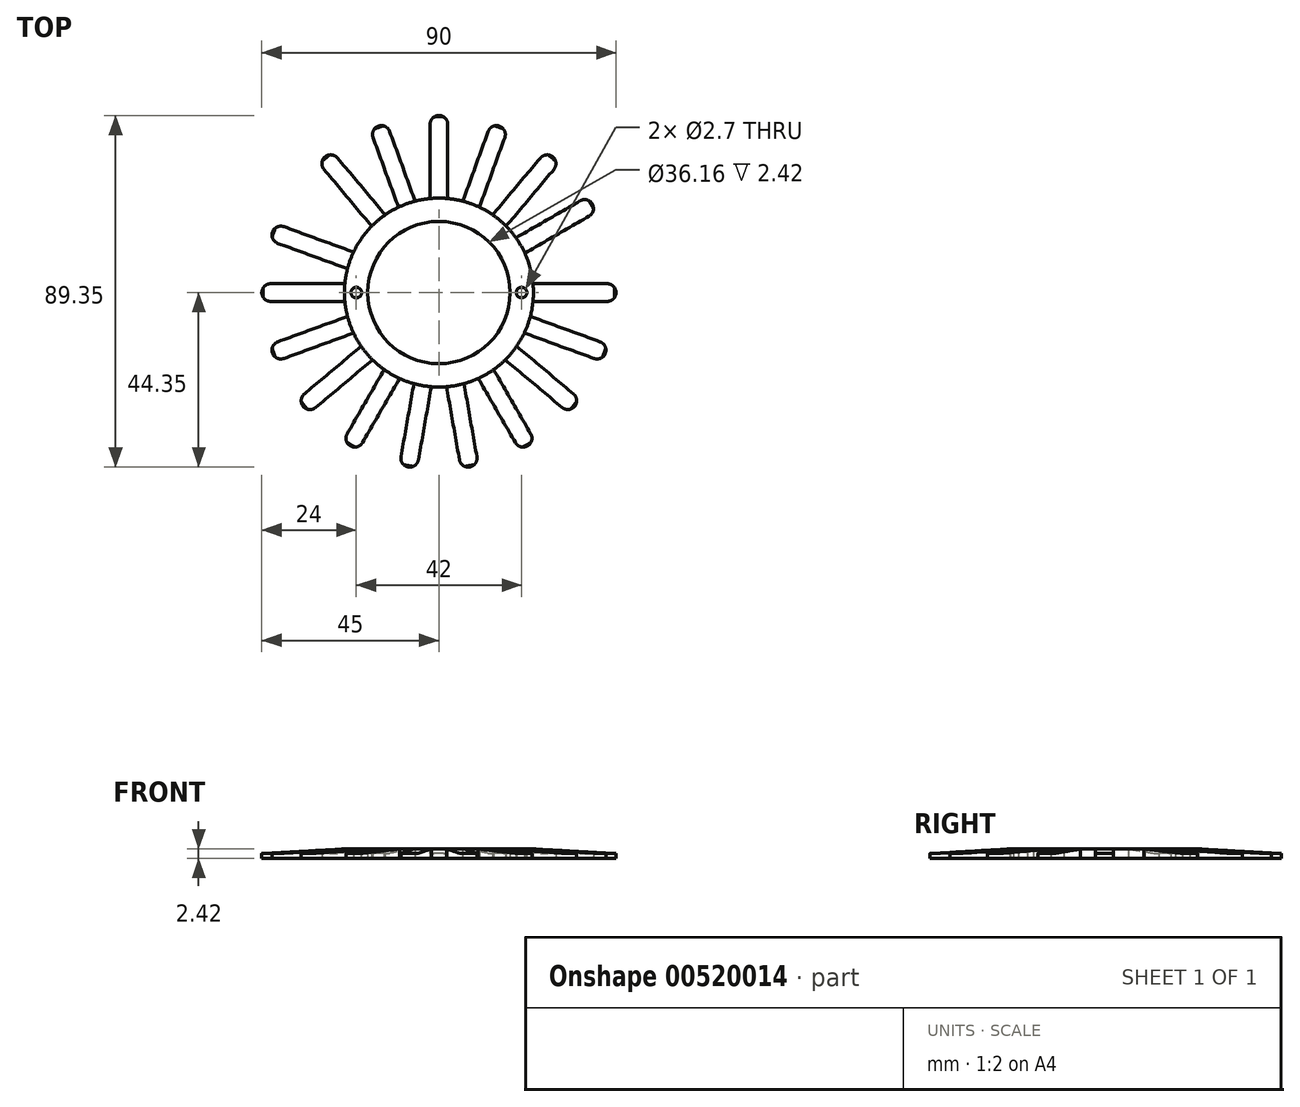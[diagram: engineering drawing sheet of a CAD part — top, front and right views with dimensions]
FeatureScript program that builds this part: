
annotation { "Feature Type Name" : "Feature", "Feature Type Description" : "" }
export const myFeature = defineFeature(function(context is Context, id is Id, definition is map)
    precondition{}
    {
        {
            var Q0;
            Q0=qCreatedBy(makeId("Top.planeOp"),FACE);
            var sketch = newSketch(context, id + "F0", { "sketchPlane" : qUnion([Q0])});
            skCircle(sketch, "E0", {"center": v(0, 0) * mm, "radius": 6.03 * mm});
            skCircle(sketch, "E1", {"center": v(0, 0) * mm, "radius": 8 * mm});
            skSolve(sketch);
        }
        {
            var Q0;
            Q0=makeQuery(id+"F0.imprint","IMPRINT",FACE,{"disambiguationData":[TD([[makeQuery(id+"F0.imprint","IMPRINT",EDGE,{"derivedFrom":sQuery(id+"F0.wireOp",EDGE,"E0")}),-1.0]])]});
            extrude(context, id + "F1", {"entities" : qUnion([Q0]), "depth" : 0.34 * mm});
        }
        {
            var Q0;
            Q0=qCreatedBy(makeId("Top.planeOp"),FACE);
            var sketch = newSketch(context, id + "F2", { "sketchPlane" : qUnion([Q0])});
            skCircle(sketch, "E2", {"center": v(0, 0) * mm, "radius": 8 * mm, "construction": true});
            skCircle(sketch, "E3", {"center": v(0, 0) * mm, "radius": 15 * mm, "construction": true});
            skArc(sketch, "E4", {"start": v(14.25, -0.75) * mm, "mid": v(15, 0) * mm, "end": v(14.25, 0.75) * mm});
            skLineSegment(sketch, "E5", {"start": v(14.25, -0.75) * mm, "end": v(7.96, -0.75) * mm});
            skLineSegment(sketch, "E6", {"start": v(14.25, 0.75) * mm, "end": v(7.96, 0.75) * mm});
            skLineSegment(sketch, "E7", {"start": v(7.96, 0.75) * mm, "end": v(7.96, -0.75) * mm});
            skSolve(sketch);
        }
        {
            var Q0;
            Q0=makeQuery(id+"F2.imprint","IMPRINT",FACE,{"disambiguationData":[TD([[makeQuery(id+"F2.imprint","IMPRINT",EDGE,{"derivedFrom":sQuery(id+"F2.wireOp",EDGE,"E4")}),1.0]])]});
            extrude(context, id + "F3", {"entities" : qUnion([Q0]), "depth" : 0.34 * mm});
        }
        {
            var Q0;
            Q0=qCreatedBy(makeId("Front.planeOp"),FACE);
            var sketch = newSketch(context, id + "F4", { "sketchPlane" : qUnion([Q0])});
            skLineSegment(sketch, "E8", {"start": v(0, 0) * mm, "end": v(0, 5.33) * mm, "construction": true});
            skSolve(sketch);
        }
        {
            var Q0;
            Q0=makeQuery(id+"F3.opExtrude","SWEPT_BODY",BODY,{"disambiguationData":[OSD([sQuery(id+"F2.wireOp",EDGE,"E4"),sQuery(id+"F2.wireOp",EDGE,"E5"),sQuery(id+"F2.wireOp",EDGE,"E6"),sQuery(id+"F2.wireOp",EDGE,"E7")])]});
            var Q1;
            Q1=sQuery(id+"F4.wireOp",EDGE,"E8");
            circularPattern(context, id + "F5", {"entities" : qUnion([Q0]), "axis" : qUnion([Q1]), "angle" : 20 * degree, "instanceCount" : 11, "oppositeDirection" : true});
        }
        {
            var Q0;
            Q0=qCreatedBy(makeId("Top.planeOp"),FACE);
            var sketch = newSketch(context, id + "F6", { "sketchPlane" : qUnion([Q0])});
            skCircle(sketch, "E9", {"center": v(0, 0) * mm, "radius": 15 * mm, "construction": true});
            skLineSegment(sketch, "E10", {"start": v(0, 0) * mm, "end": v(13, 7.5) * mm, "construction": true});
            skLineSegment(sketch, "E11", {"start": v(0, 0) * mm, "end": v(13.86, 0) * mm, "construction": true});
            skArc(sketch, "E12", {"start": v(12.72, 6.48) * mm, "mid": v(13, 7.5) * mm, "end": v(11.97, 7.77) * mm});
            skLineSegment(sketch, "E13", {"start": v(12.34, 7.13) * mm, "end": v(12.72, 6.48) * mm});
            skLineSegment(sketch, "E14", {"start": v(12.72, 6.48) * mm, "end": v(6.65, 2.98) * mm});
            skLineSegment(sketch, "E15", {"start": v(6.65, 2.98) * mm, "end": v(5.9, 4.27) * mm});
            skLineSegment(sketch, "E16", {"start": v(5.9, 4.27) * mm, "end": v(11.97, 7.77) * mm});
            skSolve(sketch);
        }
        {
            var Q0;
            Q0=makeQuery(id+"F6.imprint","IMPRINT",FACE,{"disambiguationData":[TD([[makeQuery(id+"F6.imprint","IMPRINT",EDGE,{"derivedFrom":sQuery(id+"F6.wireOp",EDGE,"E12")}),1.0]])]});
            extrude(context, id + "F7", {"entities" : qUnion([Q0]), "depth" : 0.34 * mm});
        }
        {
            var Q0;
            Q0=makeQuery(id+"F7.opExtrude","SWEPT_BODY",BODY,{"disambiguationData":[OSD([sQuery(id+"F6.wireOp",EDGE,"E12"),sQuery(id+"F6.wireOp",EDGE,"E14"),sQuery(id+"F6.wireOp",EDGE,"E15"),sQuery(id+"F6.wireOp",EDGE,"E16")])]});
            var Q1;
            Q1=sQuery(id+"F4.wireOp",EDGE,"E8");
            circularPattern(context, id + "F8", {"entities" : qUnion([Q0]), "axis" : qUnion([Q1]), "angle" : 20 * degree, "instanceCount" : 6});
        }
        {
            var Q0;
            Q0=makeQuery(id+"F1.opExtrude","SWEPT_BODY",BODY,{"disambiguationData":[OSD([sQuery(id+"F0.wireOp",EDGE,"E0"),sQuery(id+"F0.wireOp",EDGE,"E1")])]});
            var Q1;
            Q1=makeQuery(id+"F7.opExtrude","SWEPT_BODY",BODY,{"disambiguationData":[OSD([sQuery(id+"F6.wireOp",EDGE,"E12"),sQuery(id+"F6.wireOp",EDGE,"E14"),sQuery(id+"F6.wireOp",EDGE,"E15"),sQuery(id+"F6.wireOp",EDGE,"E16")])]});
            var Q2;
            Q2=makeQuery(id+"F8.opPattern","COPY",BODY,{"derivedFrom":makeQuery(id+"F7.opExtrude","SWEPT_BODY",BODY,{"disambiguationData":[OSD([sQuery(id+"F6.wireOp",EDGE,"E12"),sQuery(id+"F6.wireOp",EDGE,"E14"),sQuery(id+"F6.wireOp",EDGE,"E15"),sQuery(id+"F6.wireOp",EDGE,"E16")])]}),"instanceName":"1"});
            var Q3;
            Q3=makeQuery(id+"F8.opPattern","COPY",BODY,{"derivedFrom":makeQuery(id+"F7.opExtrude","SWEPT_BODY",BODY,{"disambiguationData":[OSD([sQuery(id+"F6.wireOp",EDGE,"E12"),sQuery(id+"F6.wireOp",EDGE,"E14"),sQuery(id+"F6.wireOp",EDGE,"E15"),sQuery(id+"F6.wireOp",EDGE,"E16")])]}),"instanceName":"2"});
            var Q4;
            Q4=makeQuery(id+"F8.opPattern","COPY",BODY,{"derivedFrom":makeQuery(id+"F7.opExtrude","SWEPT_BODY",BODY,{"disambiguationData":[OSD([sQuery(id+"F6.wireOp",EDGE,"E12"),sQuery(id+"F6.wireOp",EDGE,"E14"),sQuery(id+"F6.wireOp",EDGE,"E15"),sQuery(id+"F6.wireOp",EDGE,"E16")])]}),"instanceName":"3"});
            var Q5;
            Q5=makeQuery(id+"F8.opPattern","COPY",BODY,{"derivedFrom":makeQuery(id+"F7.opExtrude","SWEPT_BODY",BODY,{"disambiguationData":[OSD([sQuery(id+"F6.wireOp",EDGE,"E12"),sQuery(id+"F6.wireOp",EDGE,"E14"),sQuery(id+"F6.wireOp",EDGE,"E15"),sQuery(id+"F6.wireOp",EDGE,"E16")])]}),"instanceName":"4"});
            var Q6;
            Q6=makeQuery(id+"F8.opPattern","COPY",BODY,{"derivedFrom":makeQuery(id+"F7.opExtrude","SWEPT_BODY",BODY,{"disambiguationData":[OSD([sQuery(id+"F6.wireOp",EDGE,"E12"),sQuery(id+"F6.wireOp",EDGE,"E14"),sQuery(id+"F6.wireOp",EDGE,"E15"),sQuery(id+"F6.wireOp",EDGE,"E16")])]}),"instanceName":"5"});
            var Q7;
            Q7=makeQuery(id+"F5.opPattern","COPY",BODY,{"derivedFrom":makeQuery(id+"F3.opExtrude","SWEPT_BODY",BODY,{"disambiguationData":[OSD([sQuery(id+"F2.wireOp",EDGE,"E4"),sQuery(id+"F2.wireOp",EDGE,"E5"),sQuery(id+"F2.wireOp",EDGE,"E6"),sQuery(id+"F2.wireOp",EDGE,"E7")])]}),"instanceName":"10"});
            var Q8;
            Q8=makeQuery(id+"F5.opPattern","COPY",BODY,{"derivedFrom":makeQuery(id+"F3.opExtrude","SWEPT_BODY",BODY,{"disambiguationData":[OSD([sQuery(id+"F2.wireOp",EDGE,"E4"),sQuery(id+"F2.wireOp",EDGE,"E5"),sQuery(id+"F2.wireOp",EDGE,"E6"),sQuery(id+"F2.wireOp",EDGE,"E7")])]}),"instanceName":"9"});
            var Q9;
            Q9=makeQuery(id+"F5.opPattern","COPY",BODY,{"derivedFrom":makeQuery(id+"F3.opExtrude","SWEPT_BODY",BODY,{"disambiguationData":[OSD([sQuery(id+"F2.wireOp",EDGE,"E4"),sQuery(id+"F2.wireOp",EDGE,"E5"),sQuery(id+"F2.wireOp",EDGE,"E6"),sQuery(id+"F2.wireOp",EDGE,"E7")])]}),"instanceName":"8"});
            var Q10;
            Q10=makeQuery(id+"F5.opPattern","COPY",BODY,{"derivedFrom":makeQuery(id+"F3.opExtrude","SWEPT_BODY",BODY,{"disambiguationData":[OSD([sQuery(id+"F2.wireOp",EDGE,"E4"),sQuery(id+"F2.wireOp",EDGE,"E5"),sQuery(id+"F2.wireOp",EDGE,"E6"),sQuery(id+"F2.wireOp",EDGE,"E7")])]}),"instanceName":"7"});
            var Q11;
            Q11=makeQuery(id+"F5.opPattern","COPY",BODY,{"derivedFrom":makeQuery(id+"F3.opExtrude","SWEPT_BODY",BODY,{"disambiguationData":[OSD([sQuery(id+"F2.wireOp",EDGE,"E4"),sQuery(id+"F2.wireOp",EDGE,"E5"),sQuery(id+"F2.wireOp",EDGE,"E6"),sQuery(id+"F2.wireOp",EDGE,"E7")])]}),"instanceName":"6"});
            var Q12;
            Q12=makeQuery(id+"F5.opPattern","COPY",BODY,{"derivedFrom":makeQuery(id+"F3.opExtrude","SWEPT_BODY",BODY,{"disambiguationData":[OSD([sQuery(id+"F2.wireOp",EDGE,"E4"),sQuery(id+"F2.wireOp",EDGE,"E5"),sQuery(id+"F2.wireOp",EDGE,"E6"),sQuery(id+"F2.wireOp",EDGE,"E7")])]}),"instanceName":"4"});
            var Q13;
            Q13=makeQuery(id+"F5.opPattern","COPY",BODY,{"derivedFrom":makeQuery(id+"F3.opExtrude","SWEPT_BODY",BODY,{"disambiguationData":[OSD([sQuery(id+"F2.wireOp",EDGE,"E4"),sQuery(id+"F2.wireOp",EDGE,"E5"),sQuery(id+"F2.wireOp",EDGE,"E6"),sQuery(id+"F2.wireOp",EDGE,"E7")])]}),"instanceName":"5"});
            var Q14;
            Q14=makeQuery(id+"F5.opPattern","COPY",BODY,{"derivedFrom":makeQuery(id+"F3.opExtrude","SWEPT_BODY",BODY,{"disambiguationData":[OSD([sQuery(id+"F2.wireOp",EDGE,"E4"),sQuery(id+"F2.wireOp",EDGE,"E5"),sQuery(id+"F2.wireOp",EDGE,"E6"),sQuery(id+"F2.wireOp",EDGE,"E7")])]}),"instanceName":"3"});
            var Q15;
            Q15=makeQuery(id+"F5.opPattern","COPY",BODY,{"derivedFrom":makeQuery(id+"F3.opExtrude","SWEPT_BODY",BODY,{"disambiguationData":[OSD([sQuery(id+"F2.wireOp",EDGE,"E4"),sQuery(id+"F2.wireOp",EDGE,"E5"),sQuery(id+"F2.wireOp",EDGE,"E6"),sQuery(id+"F2.wireOp",EDGE,"E7")])]}),"instanceName":"2"});
            var Q16;
            Q16=makeQuery(id+"F5.opPattern","COPY",BODY,{"derivedFrom":makeQuery(id+"F3.opExtrude","SWEPT_BODY",BODY,{"disambiguationData":[OSD([sQuery(id+"F2.wireOp",EDGE,"E4"),sQuery(id+"F2.wireOp",EDGE,"E5"),sQuery(id+"F2.wireOp",EDGE,"E6"),sQuery(id+"F2.wireOp",EDGE,"E7")])]}),"instanceName":"1"});
            var Q17;
            Q17=makeQuery(id+"F3.opExtrude","SWEPT_BODY",BODY,{"disambiguationData":[OSD([sQuery(id+"F2.wireOp",EDGE,"E4"),sQuery(id+"F2.wireOp",EDGE,"E5"),sQuery(id+"F2.wireOp",EDGE,"E6"),sQuery(id+"F2.wireOp",EDGE,"E7")])]});
            booleanBodies(context, id + "F9", {"operationType" : BooleanOperationType.UNION, "tools" : qUnion([Q0, Q1, Q2, Q3, Q4, Q5, Q6, Q7, Q8, Q9, Q10, Q11, Q12, Q13, Q14, Q15, Q16, Q17])});
        }
        {
            var Q0;
            {var subQ0=makeQuery(id+"F3.opExtrude","CAP_FACE",FACE,{"disambiguationData":[OSD([sQuery(id+"F2.wireOp",EDGE,"E4"),sQuery(id+"F2.wireOp",EDGE,"E5"),sQuery(id+"F2.wireOp",EDGE,"E6"),sQuery(id+"F2.wireOp",EDGE,"E7")])],"isStart":false});var subQ1=makeQuery(id+"F7.opExtrude","CAP_FACE",FACE,{"disambiguationData":[OSD([sQuery(id+"F6.wireOp",EDGE,"E12"),sQuery(id+"F6.wireOp",EDGE,"E14"),sQuery(id+"F6.wireOp",EDGE,"E15"),sQuery(id+"F6.wireOp",EDGE,"E16")])],"isStart":false});Q0=makeQuery(id+"F9.opBoolean","MERGE",FACE,{"derivedFrom":[makeQuery(id+"F1.opExtrude","CAP_FACE",FACE,{"disambiguationData":[OSD([sQuery(id+"F0.wireOp",EDGE,"E0"),sQuery(id+"F0.wireOp",EDGE,"E1")])],"isStart":false}),subQ0,makeQuery(id+"F5.opPattern","COPY",FACE,{"derivedFrom":subQ0,"instanceName":"1"}),makeQuery(id+"F5.opPattern","COPY",FACE,{"derivedFrom":subQ0,"instanceName":"2"}),makeQuery(id+"F5.opPattern","COPY",FACE,{"derivedFrom":subQ0,"instanceName":"3"}),makeQuery(id+"F5.opPattern","COPY",FACE,{"derivedFrom":subQ0,"instanceName":"4"}),makeQuery(id+"F5.opPattern","COPY",FACE,{"derivedFrom":subQ0,"instanceName":"5"}),makeQuery(id+"F5.opPattern","COPY",FACE,{"derivedFrom":subQ0,"instanceName":"6"}),makeQuery(id+"F5.opPattern","COPY",FACE,{"derivedFrom":subQ0,"instanceName":"7"}),makeQuery(id+"F5.opPattern","COPY",FACE,{"derivedFrom":subQ0,"instanceName":"8"}),makeQuery(id+"F5.opPattern","COPY",FACE,{"derivedFrom":subQ0,"instanceName":"9"}),makeQuery(id+"F5.opPattern","COPY",FACE,{"derivedFrom":subQ0,"instanceName":"10"}),subQ1,makeQuery(id+"F8.opPattern","COPY",FACE,{"derivedFrom":subQ1,"instanceName":"1"}),makeQuery(id+"F8.opPattern","COPY",FACE,{"derivedFrom":subQ1,"instanceName":"2"}),makeQuery(id+"F8.opPattern","COPY",FACE,{"derivedFrom":subQ1,"instanceName":"3"}),makeQuery(id+"F8.opPattern","COPY",FACE,{"derivedFrom":subQ1,"instanceName":"4"}),makeQuery(id+"F8.opPattern","COPY",FACE,{"derivedFrom":subQ1,"instanceName":"5"})]});}
            var sketch = newSketch(context, id + "F10", { "sketchPlane" : qUnion([Q0])});
            skCircle(sketch, "E17", {"center": v(0, 0) * mm, "radius": 7 * mm, "construction": true});
            skCircle(sketch, "E18", {"center": v(7, 0) * mm, "radius": 0.45 * mm});
            skCircle(sketch, "E19", {"center": v(-7, 0) * mm, "radius": 0.45 * mm});
            skSolve(sketch);
        }
        {
            var Q0;
            {Q0=qUnion([makeQuery(id+"F10.imprint","IMPRINT",FACE,{"disambiguationData":[TD([[makeQuery(id+"F10.imprint","IMPRINT",EDGE,{"derivedFrom":sQuery(id+"F10.wireOp",EDGE,"E18")}),1.0]])]}),makeQuery(id+"F10.imprint","IMPRINT",FACE,{"disambiguationData":[TD([[makeQuery(id+"F10.imprint","IMPRINT",EDGE,{"derivedFrom":sQuery(id+"F10.wireOp",EDGE,"E19")}),1.0]])]})]);}
            var Q2;
            {var subQ0=makeQuery(id+"F7.opExtrude","CAP_FACE",FACE,{"disambiguationData":[OSD([sQuery(id+"F6.wireOp",EDGE,"E12"),sQuery(id+"F6.wireOp",EDGE,"E14"),sQuery(id+"F6.wireOp",EDGE,"E15"),sQuery(id+"F6.wireOp",EDGE,"E16")])],"isStart":true});var subQ1=makeQuery(id+"F3.opExtrude","CAP_FACE",FACE,{"disambiguationData":[OSD([sQuery(id+"F2.wireOp",EDGE,"E4"),sQuery(id+"F2.wireOp",EDGE,"E5"),sQuery(id+"F2.wireOp",EDGE,"E6"),sQuery(id+"F2.wireOp",EDGE,"E7")])],"isStart":true});Q2=makeQuery(id+"F9.opBoolean","MERGE",FACE,{"derivedFrom":[makeQuery(id+"F1.opExtrude","CAP_FACE",FACE,{"disambiguationData":[OSD([sQuery(id+"F0.wireOp",EDGE,"E0"),sQuery(id+"F0.wireOp",EDGE,"E1")])],"isStart":true}),subQ1,makeQuery(id+"F5.opPattern","COPY",FACE,{"derivedFrom":subQ1,"instanceName":"1"}),makeQuery(id+"F5.opPattern","COPY",FACE,{"derivedFrom":subQ1,"instanceName":"2"}),makeQuery(id+"F5.opPattern","COPY",FACE,{"derivedFrom":subQ1,"instanceName":"3"}),makeQuery(id+"F5.opPattern","COPY",FACE,{"derivedFrom":subQ1,"instanceName":"4"}),makeQuery(id+"F5.opPattern","COPY",FACE,{"derivedFrom":subQ1,"instanceName":"5"}),makeQuery(id+"F5.opPattern","COPY",FACE,{"derivedFrom":subQ1,"instanceName":"6"}),makeQuery(id+"F5.opPattern","COPY",FACE,{"derivedFrom":subQ1,"instanceName":"7"}),makeQuery(id+"F5.opPattern","COPY",FACE,{"derivedFrom":subQ1,"instanceName":"8"}),makeQuery(id+"F5.opPattern","COPY",FACE,{"derivedFrom":subQ1,"instanceName":"9"}),makeQuery(id+"F5.opPattern","COPY",FACE,{"derivedFrom":subQ1,"instanceName":"10"}),subQ0,makeQuery(id+"F8.opPattern","COPY",FACE,{"derivedFrom":subQ0,"instanceName":"1"}),makeQuery(id+"F8.opPattern","COPY",FACE,{"derivedFrom":subQ0,"instanceName":"2"}),makeQuery(id+"F8.opPattern","COPY",FACE,{"derivedFrom":subQ0,"instanceName":"3"}),makeQuery(id+"F8.opPattern","COPY",FACE,{"derivedFrom":subQ0,"instanceName":"4"}),makeQuery(id+"F8.opPattern","COPY",FACE,{"derivedFrom":subQ0,"instanceName":"5"})]});}
            extrude(context, id + "F11", {"entities" : qUnion([Q0]), "operationType" : NewBodyOperationType.REMOVE, "endBound" : BoundingType.UP_TO_SURFACE, "oppositeDirection" : true, "depth" : 0.14 * mm, "endBoundEntityFace" : qUnion([Q2])});
        }
        {
            var Q0;
            Q0=makeQuery(id+"F1.opExtrude","SWEPT_BODY",BODY,{"disambiguationData":[OSD([sQuery(id+"F0.wireOp",EDGE,"E0"),sQuery(id+"F0.wireOp",EDGE,"E1")])]});
            var Q1;
            Q1=sQuery(id+"F4.wireOp",VERTEX,"E8.start");
            transform(context, id + "F12", {"entities" : qUnion([Q0]), "transformType" : TransformType.SCALE_UNIFORMLY, "scale" : 3, "makeCopy" : false, "scalePoint" : qUnion([Q1])});
        }
        {
            var Q0;
            Q0=qCreatedBy(makeId("Front.planeOp"),FACE);
            var sketch = newSketch(context, id + "F15", { "sketchPlane" : qUnion([Q0])});
            skLineSegment(sketch, "E20", {"start": v(18, 0) * mm, "end": v(45, 0) * mm});
            skLineSegment(sketch, "E21", {"start": v(45, 1) * mm, "end": v(24, 2.22) * mm});
            skLineSegment(sketch, "E22", {"start": v(18, 2.22) * mm, "end": v(18, 0) * mm});
            skLineSegment(sketch, "E23", {"start": v(45, 0) * mm, "end": v(45, 1) * mm});
            skLineSegment(sketch, "E24", {"start": v(24, 2.22) * mm, "end": v(18, 2.22) * mm});
            skSolve(sketch);
        }
        {
            var Q0;
            Q0=qSketchRegion(id+"F15",true);
            var Q1;
            Q1=sQuery(id+"F4.wireOp",EDGE,"E8");
            revolve(context, id + "F13", {"entities" : qUnion([Q0]), "axis" : qUnion([Q1]), "revolveType" : RevolveType.FULL});
        }
        {
            var Q0;
            {var subQ0=makeQuery(id+"F7.opExtrude","CAP_FACE",FACE,{"disambiguationData":[OSD([sQuery(id+"F6.wireOp",EDGE,"E12"),sQuery(id+"F6.wireOp",EDGE,"E14"),sQuery(id+"F6.wireOp",EDGE,"E15"),sQuery(id+"F6.wireOp",EDGE,"E16")])],"isStart":true});var subQ1=makeQuery(id+"F3.opExtrude","CAP_FACE",FACE,{"disambiguationData":[OSD([sQuery(id+"F2.wireOp",EDGE,"E4"),sQuery(id+"F2.wireOp",EDGE,"E5"),sQuery(id+"F2.wireOp",EDGE,"E6"),sQuery(id+"F2.wireOp",EDGE,"E7")])],"isStart":true});Q0=makeQuery(id+"F9.opBoolean","MERGE",FACE,{"derivedFrom":[makeQuery(id+"F1.opExtrude","CAP_FACE",FACE,{"disambiguationData":[OSD([sQuery(id+"F0.wireOp",EDGE,"E0"),sQuery(id+"F0.wireOp",EDGE,"E1")])],"isStart":true}),subQ1,makeQuery(id+"F5.opPattern","COPY",FACE,{"derivedFrom":subQ1,"instanceName":"1"}),makeQuery(id+"F5.opPattern","COPY",FACE,{"derivedFrom":subQ1,"instanceName":"2"}),makeQuery(id+"F5.opPattern","COPY",FACE,{"derivedFrom":subQ1,"instanceName":"3"}),makeQuery(id+"F5.opPattern","COPY",FACE,{"derivedFrom":subQ1,"instanceName":"4"}),makeQuery(id+"F5.opPattern","COPY",FACE,{"derivedFrom":subQ1,"instanceName":"5"}),makeQuery(id+"F5.opPattern","COPY",FACE,{"derivedFrom":subQ1,"instanceName":"6"}),makeQuery(id+"F5.opPattern","COPY",FACE,{"derivedFrom":subQ1,"instanceName":"7"}),makeQuery(id+"F5.opPattern","COPY",FACE,{"derivedFrom":subQ1,"instanceName":"8"}),makeQuery(id+"F5.opPattern","COPY",FACE,{"derivedFrom":subQ1,"instanceName":"9"}),makeQuery(id+"F5.opPattern","COPY",FACE,{"derivedFrom":subQ1,"instanceName":"10"}),subQ0,makeQuery(id+"F8.opPattern","COPY",FACE,{"derivedFrom":subQ0,"instanceName":"1"}),makeQuery(id+"F8.opPattern","COPY",FACE,{"derivedFrom":subQ0,"instanceName":"2"}),makeQuery(id+"F8.opPattern","COPY",FACE,{"derivedFrom":subQ0,"instanceName":"3"}),makeQuery(id+"F8.opPattern","COPY",FACE,{"derivedFrom":subQ0,"instanceName":"4"}),makeQuery(id+"F8.opPattern","COPY",FACE,{"derivedFrom":subQ0,"instanceName":"5"})]});}
            extrude(context, id + "F16", {"entities" : qUnion([Q0]), "operationType" : NewBodyOperationType.INTERSECT, "oppositeDirection" : true, "depth" : 2.22 * mm});
        }
        {
            var Q0;
            {var subQ0=makeQuery(id+"F7.opExtrude","CAP_FACE",FACE,{"disambiguationData":[OSD([sQuery(id+"F6.wireOp",EDGE,"E12"),sQuery(id+"F6.wireOp",EDGE,"E14"),sQuery(id+"F6.wireOp",EDGE,"E15"),sQuery(id+"F6.wireOp",EDGE,"E16")])],"isStart":true});var subQ1=makeQuery(id+"F3.opExtrude","CAP_FACE",FACE,{"disambiguationData":[OSD([sQuery(id+"F2.wireOp",EDGE,"E4"),sQuery(id+"F2.wireOp",EDGE,"E5"),sQuery(id+"F2.wireOp",EDGE,"E6"),sQuery(id+"F2.wireOp",EDGE,"E7")])],"isStart":true});Q0=makeQuery(id+"F9.opBoolean","MERGE",FACE,{"derivedFrom":[makeQuery(id+"F1.opExtrude","CAP_FACE",FACE,{"disambiguationData":[OSD([sQuery(id+"F0.wireOp",EDGE,"E0"),sQuery(id+"F0.wireOp",EDGE,"E1")])],"isStart":true}),subQ1,makeQuery(id+"F5.opPattern","COPY",FACE,{"derivedFrom":subQ1,"instanceName":"1"}),makeQuery(id+"F5.opPattern","COPY",FACE,{"derivedFrom":subQ1,"instanceName":"2"}),makeQuery(id+"F5.opPattern","COPY",FACE,{"derivedFrom":subQ1,"instanceName":"3"}),makeQuery(id+"F5.opPattern","COPY",FACE,{"derivedFrom":subQ1,"instanceName":"4"}),makeQuery(id+"F5.opPattern","COPY",FACE,{"derivedFrom":subQ1,"instanceName":"5"}),makeQuery(id+"F5.opPattern","COPY",FACE,{"derivedFrom":subQ1,"instanceName":"6"}),makeQuery(id+"F5.opPattern","COPY",FACE,{"derivedFrom":subQ1,"instanceName":"7"}),makeQuery(id+"F5.opPattern","COPY",FACE,{"derivedFrom":subQ1,"instanceName":"8"}),makeQuery(id+"F5.opPattern","COPY",FACE,{"derivedFrom":subQ1,"instanceName":"9"}),makeQuery(id+"F5.opPattern","COPY",FACE,{"derivedFrom":subQ1,"instanceName":"10"}),subQ0,makeQuery(id+"F8.opPattern","COPY",FACE,{"derivedFrom":subQ0,"instanceName":"1"}),makeQuery(id+"F8.opPattern","COPY",FACE,{"derivedFrom":subQ0,"instanceName":"2"}),makeQuery(id+"F8.opPattern","COPY",FACE,{"derivedFrom":subQ0,"instanceName":"3"}),makeQuery(id+"F8.opPattern","COPY",FACE,{"derivedFrom":subQ0,"instanceName":"4"}),makeQuery(id+"F8.opPattern","COPY",FACE,{"derivedFrom":subQ0,"instanceName":"5"})]});}
            extrude(context, id + "F14", {"entities" : qUnion([Q0]), "operationType" : NewBodyOperationType.ADD, "depth" : 0.2 * mm});
        }
    });
